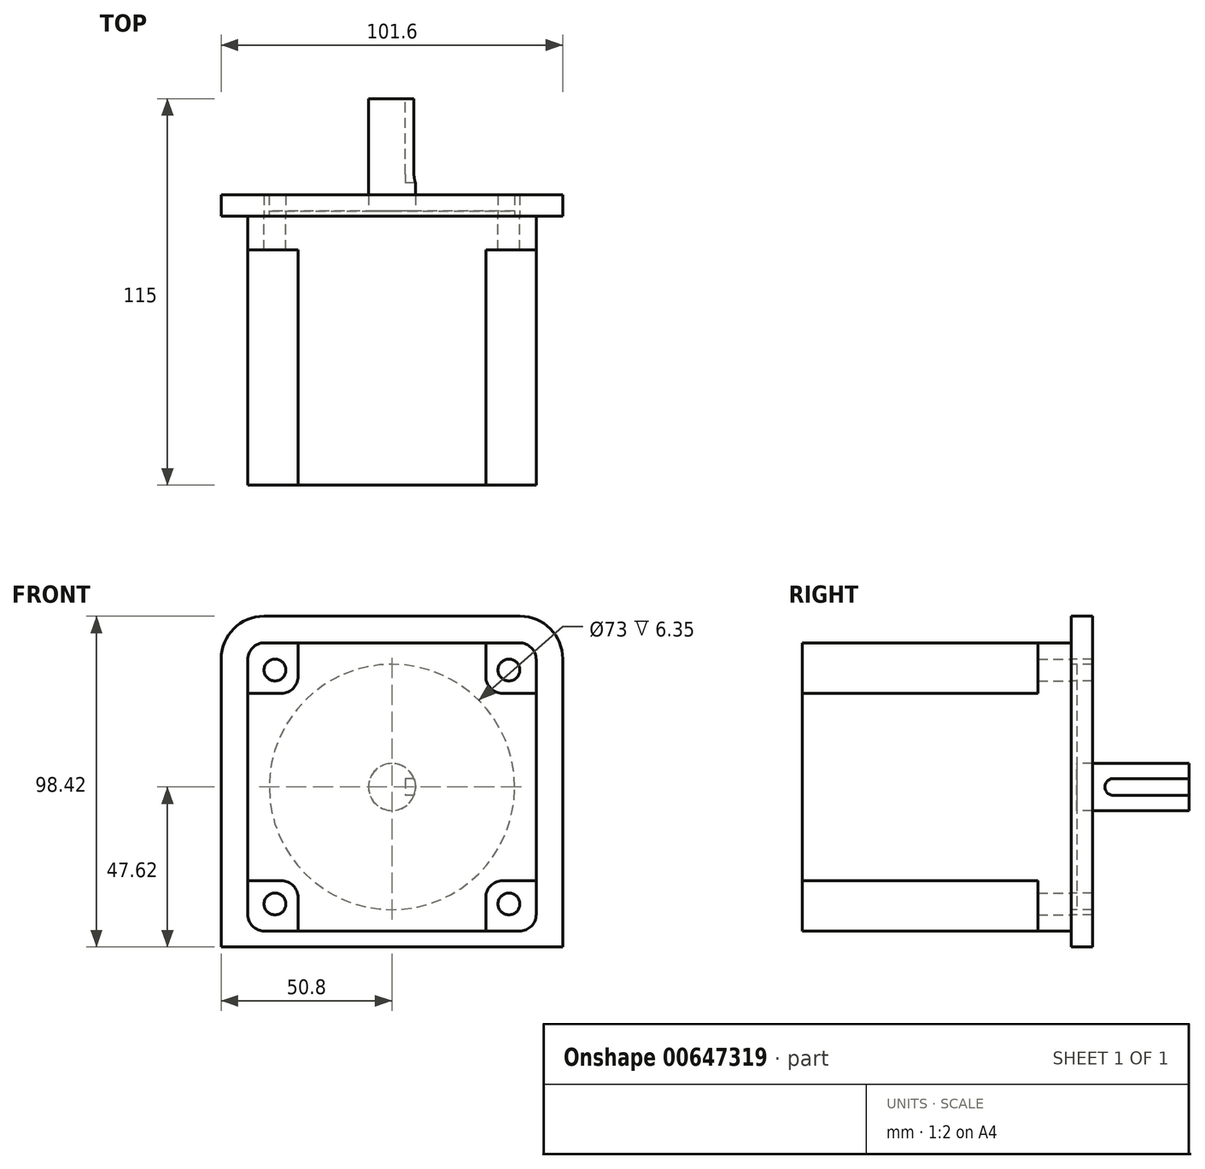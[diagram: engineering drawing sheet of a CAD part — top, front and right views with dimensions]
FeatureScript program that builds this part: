
annotation { "Feature Type Name" : "Feature", "Feature Type Description" : "" }
export const myFeature = defineFeature(function(context is Context, id is Id, definition is map)
    precondition{}
    {
        {
            var Q0;
            Q0=qCreatedBy(makeId("Front.planeOp"),FACE);
            var sketch = newSketch(context, id + "F0", { "sketchPlane" : qUnion([Q0])});
            skLineSegment(sketch, "E0.bottom", {"start": v(-37.9, 42.9) * mm, "end": v(37.9, 42.9) * mm});
            skLineSegment(sketch, "E0.top", {"start": v(-37.9, -42.9) * mm, "end": v(37.9, -42.9) * mm});
            skLineSegment(sketch, "E0.left", {"start": v(-42.9, 37.9) * mm, "end": v(-42.9, -37.9) * mm});
            skLineSegment(sketch, "E0.right", {"start": v(42.9, 37.9) * mm, "end": v(42.9, -37.9) * mm});
            skArc(sketch, "E1.filletArc", {"start": v(-42.9, -37.9) * mm, "mid": v(-41.44, -41.44) * mm, "end": v(-37.9, -42.9) * mm});
            skPoint(sketch, "E2.visualSharp", {"position": v(-42.9, 42.9) * mm});
            skArc(sketch, "E2.filletArc", {"start": v(-37.9, 42.9) * mm, "mid": v(-41.44, 41.44) * mm, "end": v(-42.9, 37.9) * mm});
            skPoint(sketch, "E3.visualSharp", {"position": v(42.9, 42.9) * mm});
            skArc(sketch, "E3.filletArc", {"start": v(42.9, 37.9) * mm, "mid": v(41.44, 41.44) * mm, "end": v(37.9, 42.9) * mm});
            skPoint(sketch, "E4.visualSharp", {"position": v(42.9, -42.9) * mm});
            skArc(sketch, "E4.filletArc", {"start": v(37.9, -42.9) * mm, "mid": v(41.44, -41.44) * mm, "end": v(42.9, -37.9) * mm});
            skSolve(sketch);
        }
        {
            var Q0;
            Q0=makeQuery(id+"F0.imprint","IMPRINT",FACE,{"disambiguationData":[TD([[makeQuery(id+"F0.imprint","IMPRINT",EDGE,{"derivedFrom":sQuery(id+"F0.wireOp",EDGE,"E0.bottom")}),-1.0]])]});
            extrude(context, id + "F1", {"entities" : qUnion([Q0]), "depth" : 80 * mm});
        }
        {
            var Q0;
            Q0=makeQuery(id+"F1.opExtrude","CAP_FACE",FACE,{"disambiguationData":[OSD([sQuery(id+"F0.wireOp",EDGE,"E0.bottom"),sQuery(id+"F0.wireOp",EDGE,"E0.top"),sQuery(id+"F0.wireOp",EDGE,"E0.left"),sQuery(id+"F0.wireOp",EDGE,"E0.right"),sQuery(id+"F0.wireOp",EDGE,"E1.filletArc"),sQuery(id+"F0.wireOp",EDGE,"E2.filletArc"),sQuery(id+"F0.wireOp",EDGE,"E3.filletArc"),sQuery(id+"F0.wireOp",EDGE,"E4.filletArc")])],"isStart":false});
            var sketch = newSketch(context, id + "F2", { "sketchPlane" : qUnion([Q0])});
            skLineSegment(sketch, "E5.bottom", {"start": v(27.9, 42.9) * mm, "end": v(42.9, 42.9) * mm});
            skLineSegment(sketch, "E5.top", {"start": v(27.9, 27.9) * mm, "end": v(42.9, 27.9) * mm});
            skLineSegment(sketch, "E5.left", {"start": v(27.9, 42.9) * mm, "end": v(27.9, 27.9) * mm});
            skLineSegment(sketch, "E5.right", {"start": v(42.9, 42.9) * mm, "end": v(42.9, 27.9) * mm});
            skLineSegment(sketch, "E6.MirrorCS", {"start": v(-27.9, 42.9) * mm, "end": v(-42.9, 42.9) * mm});
            skLineSegment(sketch, "E7.MirrorCS", {"start": v(-27.9, 27.9) * mm, "end": v(-42.9, 27.9) * mm});
            skLineSegment(sketch, "E8.MirrorCS", {"start": v(-42.9, 42.9) * mm, "end": v(-42.9, 27.9) * mm});
            skLineSegment(sketch, "E9.MirrorCS", {"start": v(-27.9, 42.9) * mm, "end": v(-27.9, 27.9) * mm});
            skLineSegment(sketch, "E10.MirrorCS", {"start": v(-27.9, -42.9) * mm, "end": v(-27.9, -27.9) * mm});
            skLineSegment(sketch, "E11.MirrorCS", {"start": v(-27.9, -42.9) * mm, "end": v(-42.9, -42.9) * mm});
            skLineSegment(sketch, "E12.MirrorCS", {"start": v(-27.9, -27.9) * mm, "end": v(-42.9, -27.9) * mm});
            skLineSegment(sketch, "E13.MirrorCS", {"start": v(-42.9, -42.9) * mm, "end": v(-42.9, -27.9) * mm});
            skLineSegment(sketch, "E14.MirrorCS", {"start": v(42.9, -42.9) * mm, "end": v(42.9, -27.9) * mm});
            skLineSegment(sketch, "E15.MirrorCS", {"start": v(27.9, -27.9) * mm, "end": v(42.9, -27.9) * mm});
            skLineSegment(sketch, "E16.MirrorCS", {"start": v(27.9, -42.9) * mm, "end": v(42.9, -42.9) * mm});
            skLineSegment(sketch, "E17.MirrorCS", {"start": v(27.9, -42.9) * mm, "end": v(27.9, -27.9) * mm});
            skSolve(sketch);
        }
        {
            var Q0;
            Q0=qSketchRegion(id+"F2",true);
            var Q1;
            Q1=makeQuery(id+"F1.opExtrude","CAP_FACE",FACE,{"disambiguationData":[OSD([sQuery(id+"F0.wireOp",EDGE,"E0.bottom"),sQuery(id+"F0.wireOp",EDGE,"E0.top"),sQuery(id+"F0.wireOp",EDGE,"E0.left"),sQuery(id+"F0.wireOp",EDGE,"E0.right"),sQuery(id+"F0.wireOp",EDGE,"E1.filletArc"),sQuery(id+"F0.wireOp",EDGE,"E2.filletArc"),sQuery(id+"F0.wireOp",EDGE,"E3.filletArc"),sQuery(id+"F0.wireOp",EDGE,"E4.filletArc")])],"isStart":false});
            extrude(context, id + "F3", {"entities" : qUnion([Q0]), "operationType" : NewBodyOperationType.REMOVE, "oppositeDirection" : true, "endBoundEntityFace" : qUnion([Q1]), "depth" : 70 * mm});
        }
        {
            var Q0;
            Q0=makeQuery(id+"F1.opExtrude","CAP_FACE",FACE,{"disambiguationData":[OSD([sQuery(id+"F0.wireOp",EDGE,"E0.bottom"),sQuery(id+"F0.wireOp",EDGE,"E0.top"),sQuery(id+"F0.wireOp",EDGE,"E0.left"),sQuery(id+"F0.wireOp",EDGE,"E0.right"),sQuery(id+"F0.wireOp",EDGE,"E1.filletArc"),sQuery(id+"F0.wireOp",EDGE,"E2.filletArc"),sQuery(id+"F0.wireOp",EDGE,"E3.filletArc"),sQuery(id+"F0.wireOp",EDGE,"E4.filletArc")])],"isStart":true});
            var sketch = newSketch(context, id + "F4", { "sketchPlane" : qUnion([Q0])});
            skCircle(sketch, "E18", {"center": v(34.8, 34.8) * mm, "radius": 3.25 * mm});
            skCircle(sketch, "E19.MirrorC", {"center": v(-34.8, 34.8) * mm, "radius": 3.25 * mm});
            skCircle(sketch, "E20.MirrorC", {"center": v(34.8, -34.8) * mm, "radius": 3.25 * mm});
            skCircle(sketch, "E21.MirrorC", {"center": v(-34.8, -34.8) * mm, "radius": 3.25 * mm});
            skSolve(sketch);
        }
        {
            var Q0;
            Q0=qSketchRegion(id+"F4",true);
            extrude(context, id + "F5", {"entities" : qUnion([Q0]), "operationType" : NewBodyOperationType.REMOVE, "endBound" : BoundingType.UP_TO_NEXT, "oppositeDirection" : true, "depth" : 25 * mm});
        }
        {
            var Q0;
            Q0=makeQuery(id+"F3.boolean.opBoolean","COPY",EDGE,{"derivedFrom":makeQuery(id+"F3.opExtrude","SWEPT_EDGE",EDGE,{"disambiguationData":[OSD([sQuery(id+"F0.wireOp",EDGE,"E0.left"),sQuery(id+"F2.wireOp",EDGE,"E8.MirrorCS"),sQuery(id+"F2.wireOp",EDGE,"E7.MirrorCS")])]})});
            var Q1;
            Q1=makeQuery(id+"F3.boolean.opBoolean","COPY",EDGE,{"derivedFrom":makeQuery(id+"F3.opExtrude","SWEPT_EDGE",EDGE,{"disambiguationData":[OSD([sQuery(id+"F0.wireOp",EDGE,"E0.left"),sQuery(id+"F2.wireOp",EDGE,"E13.MirrorCS"),sQuery(id+"F2.wireOp",EDGE,"E12.MirrorCS")])]})});
            var Q2;
            Q2=makeQuery(id+"F3.boolean.opBoolean","COPY",EDGE,{"derivedFrom":makeQuery(id+"F3.opExtrude","SWEPT_EDGE",EDGE,{"disambiguationData":[OSD([sQuery(id+"F2.wireOp",EDGE,"E12.MirrorCS"),sQuery(id+"F2.wireOp",EDGE,"E10.MirrorCS")])]})});
            var Q3;
            Q3=makeQuery(id+"F3.boolean.opBoolean","COPY",EDGE,{"derivedFrom":makeQuery(id+"F3.opExtrude","SWEPT_EDGE",EDGE,{"disambiguationData":[OSD([sQuery(id+"F0.wireOp",EDGE,"E0.top"),sQuery(id+"F2.wireOp",EDGE,"E10.MirrorCS"),sQuery(id+"F2.wireOp",EDGE,"E11.MirrorCS")])]})});
            var Q4;
            Q4=makeQuery(id+"F3.boolean.opBoolean","COPY",EDGE,{"derivedFrom":makeQuery(id+"F3.opExtrude","SWEPT_EDGE",EDGE,{"disambiguationData":[OSD([sQuery(id+"F0.wireOp",EDGE,"E0.top"),sQuery(id+"F2.wireOp",EDGE,"E17.MirrorCS"),sQuery(id+"F2.wireOp",EDGE,"E16.MirrorCS")])]})});
            var Q5;
            Q5=makeQuery(id+"F3.boolean.opBoolean","COPY",EDGE,{"derivedFrom":makeQuery(id+"F3.opExtrude","SWEPT_EDGE",EDGE,{"disambiguationData":[OSD([sQuery(id+"F0.wireOp",EDGE,"E0.bottom"),sQuery(id+"F2.wireOp",EDGE,"E9.MirrorCS"),sQuery(id+"F2.wireOp",EDGE,"E6.MirrorCS")])]})});
            var Q6;
            Q6=makeQuery(id+"F3.boolean.opBoolean","COPY",EDGE,{"derivedFrom":makeQuery(id+"F3.opExtrude","SWEPT_EDGE",EDGE,{"disambiguationData":[OSD([sQuery(id+"F2.wireOp",EDGE,"E17.MirrorCS"),sQuery(id+"F2.wireOp",EDGE,"E15.MirrorCS")])]})});
            var Q7;
            Q7=makeQuery(id+"F3.boolean.opBoolean","COPY",EDGE,{"derivedFrom":makeQuery(id+"F3.opExtrude","SWEPT_EDGE",EDGE,{"disambiguationData":[OSD([sQuery(id+"F0.wireOp",EDGE,"E0.right"),sQuery(id+"F2.wireOp",EDGE,"E14.MirrorCS"),sQuery(id+"F2.wireOp",EDGE,"E15.MirrorCS")])]})});
            var Q8;
            Q8=makeQuery(id+"F3.boolean.opBoolean","COPY",EDGE,{"derivedFrom":makeQuery(id+"F3.opExtrude","SWEPT_EDGE",EDGE,{"disambiguationData":[OSD([sQuery(id+"F0.wireOp",EDGE,"E0.right"),sQuery(id+"F2.wireOp",EDGE,"E5.right"),sQuery(id+"F2.wireOp",EDGE,"E5.top")])]})});
            var Q9;
            Q9=makeQuery(id+"F3.boolean.opBoolean","COPY",EDGE,{"derivedFrom":makeQuery(id+"F3.opExtrude","SWEPT_EDGE",EDGE,{"disambiguationData":[OSD([sQuery(id+"F0.wireOp",EDGE,"E0.bottom"),sQuery(id+"F2.wireOp",EDGE,"E5.bottom"),sQuery(id+"F2.wireOp",EDGE,"E5.left")])]})});
            var Q10;
            Q10=makeQuery(id+"F3.boolean.opBoolean","COPY",EDGE,{"derivedFrom":makeQuery(id+"F3.opExtrude","SWEPT_EDGE",EDGE,{"disambiguationData":[OSD([sQuery(id+"F2.wireOp",EDGE,"E5.top"),sQuery(id+"F2.wireOp",EDGE,"E5.left")])]})});
            var Q11;
            Q11=makeQuery(id+"F3.boolean.opBoolean","COPY",EDGE,{"derivedFrom":makeQuery(id+"F3.opExtrude","SWEPT_EDGE",EDGE,{"disambiguationData":[OSD([sQuery(id+"F2.wireOp",EDGE,"E9.MirrorCS"),sQuery(id+"F2.wireOp",EDGE,"E7.MirrorCS")])]})});
            fillet(context, id + "F6", {"entities" : qUnion([Q0, Q1, Q2, Q3, Q4, Q5, Q6, Q7, Q8, Q9, Q10, Q11]), "radius" : 5 * mm, "tangentPropagation" : true, "allowEdgeOverflow" : false});
        }
        {
            var Q0;
            Q0=makeQuery(id+"F1.opExtrude","CAP_FACE",FACE,{"disambiguationData":[OSD([sQuery(id+"F0.wireOp",EDGE,"E0.bottom"),sQuery(id+"F0.wireOp",EDGE,"E0.top"),sQuery(id+"F0.wireOp",EDGE,"E0.left"),sQuery(id+"F0.wireOp",EDGE,"E0.right"),sQuery(id+"F0.wireOp",EDGE,"E1.filletArc"),sQuery(id+"F0.wireOp",EDGE,"E2.filletArc"),sQuery(id+"F0.wireOp",EDGE,"E3.filletArc"),sQuery(id+"F0.wireOp",EDGE,"E4.filletArc")])],"isStart":true});
            var sketch = newSketch(context, id + "F7", { "sketchPlane" : qUnion([Q0])});
            skCircle(sketch, "E22", {"center": v(0, 0) * mm, "radius": 36.5 * mm});
            skSolve(sketch);
        }
        {
            var Q0;
            Q0=qSketchRegion(id+"F7",true);
            extrude(context, id + "F8", {"entities" : qUnion([Q0]), "operationType" : NewBodyOperationType.ADD, "depth" : 1.6 * mm});
        }
        {
            var Q0;
            Q0=makeQuery(id+"F1.opExtrude","CAP_FACE",FACE,{"disambiguationData":[OSD([sQuery(id+"F0.wireOp",EDGE,"E0.bottom"),sQuery(id+"F0.wireOp",EDGE,"E0.top"),sQuery(id+"F0.wireOp",EDGE,"E0.left"),sQuery(id+"F0.wireOp",EDGE,"E0.right"),sQuery(id+"F0.wireOp",EDGE,"E1.filletArc"),sQuery(id+"F0.wireOp",EDGE,"E2.filletArc"),sQuery(id+"F0.wireOp",EDGE,"E3.filletArc"),sQuery(id+"F0.wireOp",EDGE,"E4.filletArc")])],"isStart":true});
            var sketch = newSketch(context, id + "F9", { "sketchPlane" : qUnion([Q0])});
            skCircle(sketch, "E23", {"center": v(0, 0) * mm, "radius": 7 * mm});
            skSolve(sketch);
        }
        {
            var Q0;
            Q0=qSketchRegion(id+"F9",true);
            var Q1;
            Q1=sQuery(id+"F9.wireOp",EDGE,"E23");
            extrude(context, id + "F10", {"entities" : qUnion([Q0]), "operationType" : NewBodyOperationType.ADD, "surfaceEntities" : qUnion([Q1]), "depth" : 35 * mm});
        }
        {
            var Q0;
            Q0=qCreatedBy(makeId("Right.planeOp"),FACE);
            cPlane(context, id + "F11", {"entities" : qUnion([Q0]), "cplaneType" : CPlaneType.OFFSET, "offset" : 4 * mm, "width" : 150 * mm, "height" : 150 * mm});
        }
        {
            var Q0;
            Q0=qCreatedBy(id+"F11.planeOp",FACE);
            var sketch = newSketch(context, id + "F12", { "sketchPlane" : qUnion([Q0])});
            skLineSegment(sketch, "E24.top", {"start": v(12.5, 2.5) * mm, "end": v(35, 2.5) * mm});
            skLineSegment(sketch, "E24.left", {"start": v(10, 0) * mm, "end": v(10, 0) * mm});
            skLineSegment(sketch, "E24.right", {"start": v(35, 0) * mm, "end": v(35, 2.5) * mm});
            skPoint(sketch, "E25.visualSharp", {"position": v(10, 2.5) * mm});
            skArc(sketch, "E25.filletArc", {"start": v(12.5, 2.5) * mm, "mid": v(10.73, 1.77) * mm, "end": v(10, 0) * mm});
            skArc(sketch, "E26.MirrorCS", {"start": v(12.5, -2.5) * mm, "mid": v(10.73, -1.77) * mm, "end": v(10, 0) * mm});
            skLineSegment(sketch, "E27.MirrorCS", {"start": v(35, 0) * mm, "end": v(35, -2.5) * mm});
            skLineSegment(sketch, "E28.MirrorCS", {"start": v(12.5, -2.5) * mm, "end": v(35, -2.5) * mm});
            skPoint(sketch, "E29.MirrorP", {"position": v(10, -2.5) * mm});
            skSolve(sketch);
        }
        {
            var Q0;
            Q0=qSketchRegion(id+"F12",true);
            extrude(context, id + "F13", {"entities" : qUnion([Q0]), "operationType" : NewBodyOperationType.REMOVE, "depth" : 5 * mm});
        }
        {
            var Q0;
            Q0=makeQuery(id+"F1.opExtrude","CAP_FACE",FACE,{"disambiguationData":[OSD([sQuery(id+"F0.wireOp",EDGE,"E0.bottom"),sQuery(id+"F0.wireOp",EDGE,"E0.top"),sQuery(id+"F0.wireOp",EDGE,"E0.left"),sQuery(id+"F0.wireOp",EDGE,"E0.right"),sQuery(id+"F0.wireOp",EDGE,"E1.filletArc"),sQuery(id+"F0.wireOp",EDGE,"E2.filletArc"),sQuery(id+"F0.wireOp",EDGE,"E3.filletArc"),sQuery(id+"F0.wireOp",EDGE,"E4.filletArc")])],"isStart":true});
            var sketch = newSketch(context, id + "F14", { "sketchPlane" : qUnion([Q0])});
            skCircle(sketch, "E30.3", {"center": v(-34.8, 34.8) * mm, "radius": 3.25 * mm});
            skCircle(sketch, "E30.4", {"center": v(0, 0) * mm, "radius": 36.5 * mm});
            skCircle(sketch, "E30.5", {"center": v(34.8, 34.8) * mm, "radius": 3.25 * mm});
            skCircle(sketch, "E30.6", {"center": v(34.8, -34.8) * mm, "radius": 3.25 * mm});
            skCircle(sketch, "E30.7", {"center": v(-34.8, -34.8) * mm, "radius": 3.25 * mm});
            skLineSegment(sketch, "E31", {"start": v(-50.8, 50.8) * mm, "end": v(-50.8, -47.63) * mm});
            skLineSegment(sketch, "E32", {"start": v(50.8, 50.8) * mm, "end": v(50.8, -47.62) * mm});
            skLineSegment(sketch, "E33", {"start": v(-50.8, 50.8) * mm, "end": v(50.8, 50.8) * mm});
            skLineSegment(sketch, "E34", {"start": v(50.8, -47.62) * mm, "end": v(-50.8, -47.63) * mm});
            skSolve(sketch);
        }
        {
            var Q0;
            Q0 = qSketchRegion(id + "F14", true);
            extrude(context, id + "F15", {"entities" : qUnion([Q0]), "depth" : 6.35 * mm, "offsetDistance" : 25.4 * mm});
        }
        {
            var Q0;
            Q0=makeQuery(id+"F15.opExtrude","SWEPT_EDGE",EDGE,{"disambiguationData":[OSD([sQuery(id+"F14.wireOp",EDGE,"E32"),sQuery(id+"F14.wireOp",EDGE,"E33")])]});
            var Q1;
            Q1=makeQuery(id+"F15.opExtrude","SWEPT_EDGE",EDGE,{"disambiguationData":[OSD([sQuery(id+"F14.wireOp",EDGE,"E31"),sQuery(id+"F14.wireOp",EDGE,"E33")])]});
            fillet(context, id + "F16", {"entities" : qUnion([Q0, Q1]), "radius" : 12.7 * mm, "tangentPropagation" : true, "allowEdgeOverflow" : false});
        }
    });
